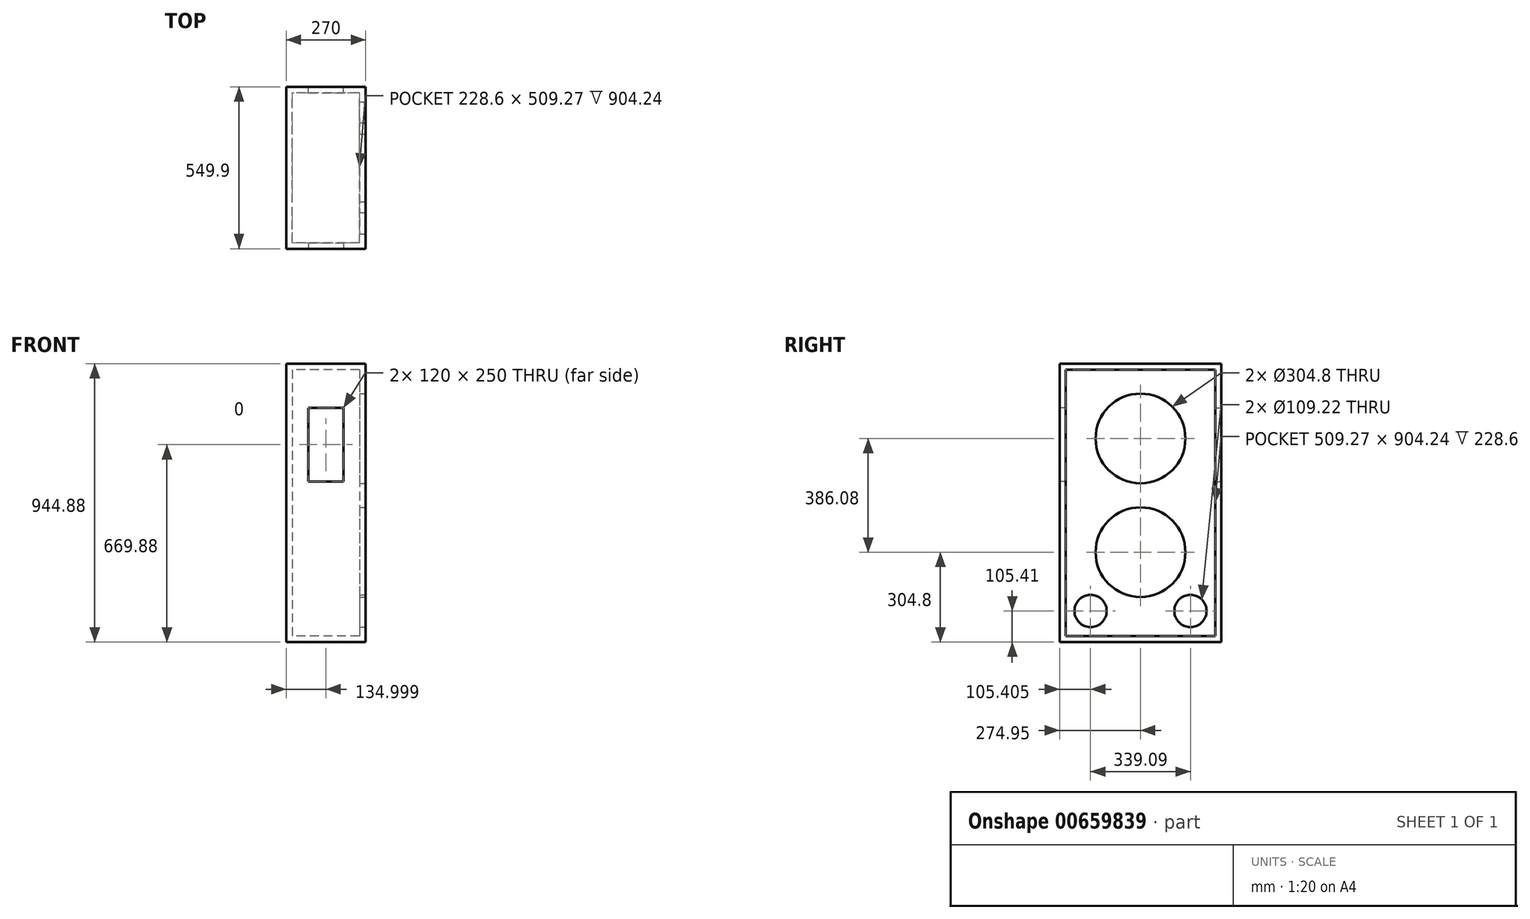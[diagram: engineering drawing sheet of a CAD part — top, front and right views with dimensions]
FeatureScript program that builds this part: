
annotation { "Feature Type Name" : "Feature", "Feature Type Description" : "" }
export const myFeature = defineFeature(function(context is Context, id is Id, definition is map)
    precondition{}
    {
        {
            var Q0;
            Q0=qCreatedBy(makeId("Top.planeOp"),FACE);
            var sketch = newSketch(context, id + "F0", { "sketchPlane" : qUnion([Q0])});
            skLineSegment(sketch, "E0.bottom", {"start": v(135, -274.95) * mm, "end": v(-135, -274.95) * mm});
            skLineSegment(sketch, "E0.top", {"start": v(135, 274.95) * mm, "end": v(-135, 274.95) * mm});
            skLineSegment(sketch, "E0.left", {"start": v(135, -274.95) * mm, "end": v(135, 274.96) * mm});
            skLineSegment(sketch, "E0.right", {"start": v(-135, -274.95) * mm, "end": v(-135, 274.96) * mm});
            skPoint(sketch, "E0.middle", {"position": v(0, 0) * mm});
            skSolve(sketch);
        }
        {
            var Q0;
            Q0 = qSketchRegion(id + "F0", true);
            extrude(context, id + "F1", {"entities" : qUnion([Q0]), "depth" : 25.4 * mm, "offsetDistance" : 25.4 * mm});
        }
        {
            var Q0;
            Q0=makeQuery(id+"F1.opExtrude","CAP_FACE",FACE,{"disambiguationData":[OSD([sQuery(id+"F0.wireOp",EDGE,"E0.bottom"),sQuery(id+"F0.wireOp",EDGE,"E0.top"),sQuery(id+"F0.wireOp",EDGE,"E0.left"),sQuery(id+"F0.wireOp",EDGE,"E0.right")])],"isStart":false});
            var sketch = newSketch(context, id + "F2", { "sketchPlane" : qUnion([Q0])});
            skSolve(sketch);
        }
        {
            var Q0;
            Q0=makeQuery(id+"F2.imprint","IMPRINT",FACE,{"disambiguationData":[TD([[makeQuery(id+"F2.imprint","IMPRINT",EDGE,{"derivedFrom":makeQuery(id+"F1.opExtrude","CAP_EDGE",EDGE,{"disambiguationData":[OSD([sQuery(id+"F0.wireOp",EDGE,"E0.bottom")])],"isStart":false})}),-1.0]])]});
            extrude(context, id + "F3", {"entities" : qUnion([Q0]), "operationType" : NewBodyOperationType.ADD, "depth" : 919.48 * mm, "offsetDistance" : 25.4 * mm});
        }
        {
            var Q0;
            {var subQ0=sQuery(id+"F0.wireOp",EDGE,"E0.left");Q0=makeQuery(id+"F3.boolean.opBoolean","MERGE",FACE,{"derivedFrom":[makeQuery(id+"F1.opExtrude","SWEPT_FACE",FACE,{"disambiguationData":[OSD([subQ0])]}),makeQuery(id+"F3.opExtrude","SWEPT_FACE",FACE,{"disambiguationData":[OSD([subQ0])]})]});}
            shell(context, id + "F4", {"entities" : qUnion([Q0]), "thickness" : 20.32 * mm});
        }
        {
            var Q0;
            Q0=makeQuery(id+"F4.opShell","OFFSET_FACE",FACE,{"disambiguationData":[OSD([sQuery(id+"F0.wireOp",EDGE,"E0.right")])]});
            extrude(context, id + "F5", {"entities" : qUnion([Q0]), "operationType" : NewBodyOperationType.ADD, "depth" : 248.92 * mm, "offsetDistance" : 25.4 * mm, "hasSecondDirection" : true, "secondDirectionOppositeDirection" : false, "secondDirectionDepth" : 228.6 * mm});
        }
        {
            var Q0;
            Q0=makeQuery(id+"F5.opExtrude","CAP_FACE",FACE,{"disambiguationData":[OSD([sQuery(id+"F0.wireOp",EDGE,"E0.right")])],"isStart":false});
            var sketch = newSketch(context, id + "F6", { "sketchPlane" : qUnion([Q0])});
            skCircle(sketch, "E1", {"center": v(0, 690.88) * mm, "radius": 152.4 * mm});
            skPoint(sketch, "E1.centerSnap0", {"position": v(0, 924.56) * mm});
            skLineSegment(sketch, "E2", {"start": v(0, 690.88) * mm, "end": v(0, -15.75) * mm, "construction": true});
            skLineSegment(sketch, "E3", {"start": v(0, 690.88) * mm, "end": v(0, 924.56) * mm});
            skSolve(sketch);
        }
        {
            var Q0;
            Q0=makeQuery(id+"F6.imprint","IMPRINT",FACE,{"disambiguationData":[TD([[makeQuery(id+"F6.imprint","IMPRINT",EDGE,{"derivedFrom":sQuery(id+"F6.wireOp",EDGE,"E1")}),1.0]])]});
            extrude(context, id + "F7", {"entities" : qUnion([Q0]), "operationType" : NewBodyOperationType.REMOVE, "oppositeDirection" : true, "depth" : 25.4 * mm, "offsetDistance" : 25.4 * mm});
        }
        {
            var Q0;
            Q0=makeQuery(id+"F5.opExtrude","CAP_FACE",FACE,{"disambiguationData":[OSD([sQuery(id+"F0.wireOp",EDGE,"E0.right")])],"isStart":false});
            var sketch = newSketch(context, id + "F8", { "sketchPlane" : qUnion([Q0])});
            skCircle(sketch, "E4", {"center": v(0, 304.8) * mm, "radius": 152.4 * mm});
            skLineSegment(sketch, "E5", {"start": v(0, 304.8) * mm, "end": v(0, 956.33) * mm, "construction": true});
            skSolve(sketch);
        }
        {
            var Q0;
            Q0 = qSketchRegion(id + "F8", true);
            extrude(context, id + "F9", {"entities" : qUnion([Q0]), "operationType" : NewBodyOperationType.REMOVE, "oppositeDirection" : true, "depth" : 25.4 * mm, "offsetDistance" : 25.4 * mm});
        }
        {
            var Q0;
            Q0=makeQuery(id+"F5.opExtrude","CAP_FACE",FACE,{"disambiguationData":[OSD([sQuery(id+"F0.wireOp",EDGE,"E0.right")])],"isStart":false});
            var sketch = newSketch(context, id + "F10", { "sketchPlane" : qUnion([Q0])});
            skCircle(sketch, "E6", {"center": v(-169.54, 105.4) * mm, "radius": 54.61 * mm});
            skSolve(sketch);
        }
        {
            var Q0;
            Q0=makeQuery(id+"F10.imprint","IMPRINT",FACE,{"disambiguationData":[TD([[makeQuery(id+"F10.imprint","IMPRINT",EDGE,{"derivedFrom":sQuery(id+"F10.wireOp",EDGE,"E6")}),1.0]])]});
            var Q1;
            Q1=sQuery(id+"F10.wireOp",EDGE,"E6");
            extrude(context, id + "F11", {"entities" : qUnion([Q0]), "operationType" : NewBodyOperationType.REMOVE, "surfaceEntities" : qUnion([Q1]), "oppositeDirection" : true, "depth" : 25.4 * mm, "offsetDistance" : 25.4 * mm});
        }
        {
            var Q0;
            Q0=makeQuery(id+"F5.opExtrude","CAP_FACE",FACE,{"disambiguationData":[OSD([sQuery(id+"F0.wireOp",EDGE,"E0.right")])],"isStart":false});
            var sketch = newSketch(context, id + "F12", { "sketchPlane" : qUnion([Q0])});
            skCircle(sketch, "E7", {"center": v(169.55, 105.4) * mm, "radius": 54.6 * mm});
            skSolve(sketch);
        }
        {
            var Q0;
            Q0=makeQuery(id+"F12.imprint","IMPRINT",FACE,{"disambiguationData":[TD([[makeQuery(id+"F12.imprint","IMPRINT",EDGE,{"derivedFrom":sQuery(id+"F12.wireOp",EDGE,"E7")}),1.0]])]});
            var Q1;
            Q1=sQuery(id+"F12.wireOp",EDGE,"E7");
            extrude(context, id + "F13", {"entities" : qUnion([Q0]), "operationType" : NewBodyOperationType.REMOVE, "surfaceEntities" : qUnion([Q1]), "oppositeDirection" : true, "depth" : 25.4 * mm, "offsetDistance" : 25.4 * mm});
        }
        {
            var Q0;
            {var subQ0=sQuery(id+"F0.wireOp",EDGE,"E0.bottom");Q0=makeQuery(id+"F3.boolean.opBoolean","MERGE",FACE,{"derivedFrom":[makeQuery(id+"F1.opExtrude","SWEPT_FACE",FACE,{"disambiguationData":[OSD([subQ0])]}),makeQuery(id+"F3.opExtrude","SWEPT_FACE",FACE,{"disambiguationData":[OSD([subQ0])]})]});}
            var sketch = newSketch(context, id + "F14", { "sketchPlane" : qUnion([Q0])});
            skLineSegment(sketch, "E8.bottom", {"start": v(-60, 794.88) * mm, "end": v(60, 794.88) * mm});
            skLineSegment(sketch, "E8.top", {"start": v(-60, 544.88) * mm, "end": v(60, 544.88) * mm});
            skLineSegment(sketch, "E8.left", {"start": v(-60, 794.88) * mm, "end": v(-60, 544.88) * mm});
            skLineSegment(sketch, "E8.right", {"start": v(60, 794.88) * mm, "end": v(60, 544.88) * mm});
            skSolve(sketch);
        }
        {
            var Q0;
            Q0=makeQuery(id+"F14.imprint","IMPRINT",FACE,{"disambiguationData":[TD([[makeQuery(id+"F14.imprint","IMPRINT",EDGE,{"derivedFrom":sQuery(id+"F14.wireOp",EDGE,"E8.bottom")}),-1.0]])]});
            extrude(context, id + "F15", {"entities" : qUnion([Q0]), "operationType" : NewBodyOperationType.ADD, "oppositeDirection" : true, "depth" : 22 * mm, "offsetDistance" : 25.4 * mm});
        }
        {
            var Q0;
            Q0=makeQuery(id+"F14.imprint","IMPRINT",FACE,{"disambiguationData":[TD([[makeQuery(id+"F14.imprint","IMPRINT",EDGE,{"derivedFrom":sQuery(id+"F14.wireOp",EDGE,"E8.bottom")}),-1.0]])]});
            extrude(context, id + "F16", {"entities" : qUnion([Q0]), "operationType" : NewBodyOperationType.REMOVE, "oppositeDirection" : true, "depth" : 55.88 * mm, "offsetDistance" : 25.4 * mm});
        }
        {
            var Q0;
            {var subQ0=sQuery(id+"F0.wireOp",EDGE,"E0.top");Q0=makeQuery(id+"F3.boolean.opBoolean","MERGE",FACE,{"derivedFrom":[makeQuery(id+"F1.opExtrude","SWEPT_FACE",FACE,{"disambiguationData":[OSD([subQ0])]}),makeQuery(id+"F3.opExtrude","SWEPT_FACE",FACE,{"disambiguationData":[OSD([subQ0])]})]});}
            var sketch = newSketch(context, id + "F17", { "sketchPlane" : qUnion([Q0])});
            skLineSegment(sketch, "E9.bottom", {"start": v(-60, 794.88) * mm, "end": v(60, 794.88) * mm});
            skLineSegment(sketch, "E9.top", {"start": v(-60, 544.88) * mm, "end": v(60, 544.88) * mm});
            skLineSegment(sketch, "E9.left", {"start": v(-60, 794.88) * mm, "end": v(-60, 544.88) * mm});
            skLineSegment(sketch, "E9.right", {"start": v(60, 794.88) * mm, "end": v(60, 544.88) * mm});
            skSolve(sketch);
        }
        {
            var Q0;
            Q0=makeQuery(id+"F17.imprint","IMPRINT",FACE,{"disambiguationData":[TD([[makeQuery(id+"F17.imprint","IMPRINT",EDGE,{"derivedFrom":sQuery(id+"F17.wireOp",EDGE,"E9.bottom")}),-1.0]])]});
            extrude(context, id + "F18", {"entities" : qUnion([Q0]), "operationType" : NewBodyOperationType.REMOVE, "oppositeDirection" : true, "depth" : 50.8 * mm, "offsetDistance" : 25.4 * mm});
        }
    });
